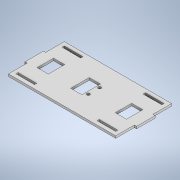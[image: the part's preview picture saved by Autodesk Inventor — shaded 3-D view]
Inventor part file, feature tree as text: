
AUTODESK INVENTOR PART (.ipt)
format: ipt  version: 2020 (Build 240168000, 168)  size: 182,272 bytes
history: native  units: in
note: dims shown in document units (in); Inventor stores cm internally (conversion verified against a paired STEP export)
features: extrude x4, sketch x4
ambient origin geometry x8: Origin, YZ Plane, XZ Plane, XY Plane, X Axis, Y Axis, Z Axis, Center Point
bodies: Solid1 (feature_tree)
feature tree (8):
  extrude  "Extrusion1"  Depth=1.1811in TaperAngle=0.0deg
  extrude  "Extrusion2"  Depth=0.8661in
  extrude  "Extrusion3"  Depth=0.5906in
  extrude  "Extrusion4"  Depth=0.3937in
  sketch  "Sketch1"  dims[d9=0.1181in d10=0.0in d30=1.1811in d31=0.0in]
  sketch  "Sketch2"  dims[d56=0.5906in d57=0.8661in]
  sketch  "Sketch3"  dims[d59=0.9843in d60=0.5906in]
  sketch  "Sketch4"  dims[d61=0.1575in d62=0.1575in d63=0.5906in d64=0.8661in d65=0.3937in d66=0.0in d67=0.5906in d68=0.5906in d69=0.3937in d70=0.0in]
